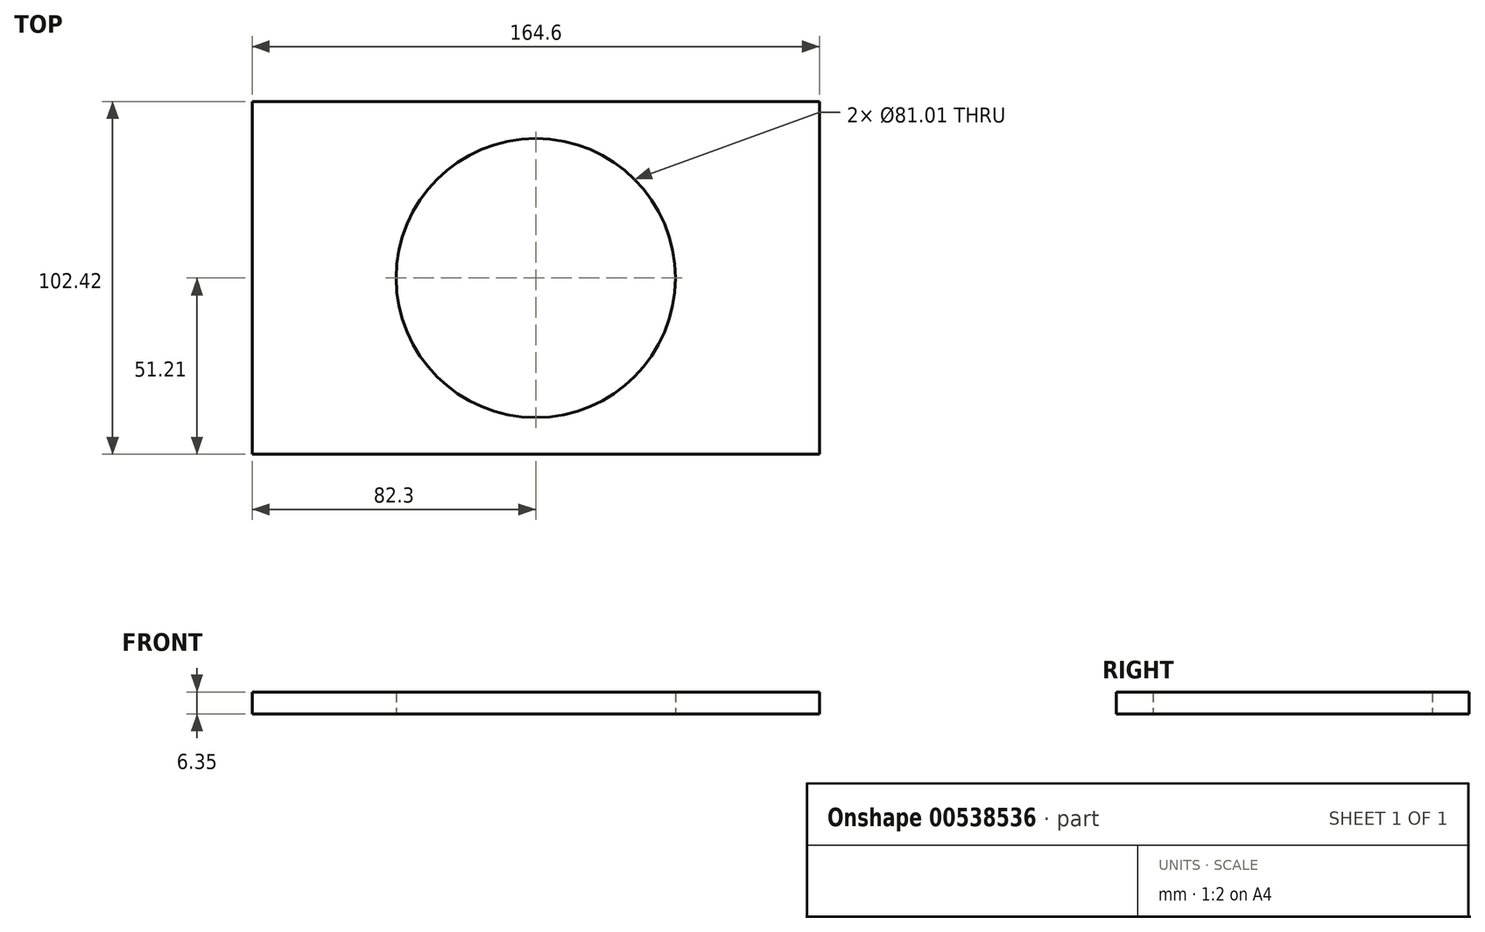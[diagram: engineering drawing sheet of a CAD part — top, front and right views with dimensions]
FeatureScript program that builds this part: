
annotation { "Feature Type Name" : "Feature", "Feature Type Description" : "" }
export const myFeature = defineFeature(function(context is Context, id is Id, definition is map)
    precondition{}
    {
        {
            var Q0;
            Q0=qCreatedBy(makeId("Top.planeOp"),FACE);
            var sketch = newSketch(context, id + "F0", { "sketchPlane" : qUnion([Q0])});
            skLineSegment(sketch, "E0.bottom", {"start": v(-82.3, 51.2) * mm, "end": v(82.3, 51.2) * mm});
            skLineSegment(sketch, "E0.top", {"start": v(-82.3, -51.2) * mm, "end": v(82.3, -51.2) * mm});
            skLineSegment(sketch, "E0.left", {"start": v(-82.3, 51.2) * mm, "end": v(-82.3, -51.2) * mm});
            skLineSegment(sketch, "E0.right", {"start": v(82.3, 51.2) * mm, "end": v(82.3, -51.2) * mm});
            skPoint(sketch, "E0.middle", {"position": v(0, 0) * mm});
            skCircle(sketch, "E1", {"center": v(0, 0) * mm, "radius": 40.5 * mm});
            skSolve(sketch);
        }
        {
            var Q0;
            Q0=makeQuery(id+"F0.imprint","IMPRINT",FACE,{"disambiguationData":[TD([[makeQuery(id+"F0.imprint","IMPRINT",EDGE,{"derivedFrom":sQuery(id+"F0.wireOp",EDGE,"E0.bottom")}),-1.0]])]});
            extrude(context, id + "F1", {"entities" : qUnion([Q0]), "depth" : 6.35 * mm, "offsetDistance" : 25.4 * mm});
        }
    });
